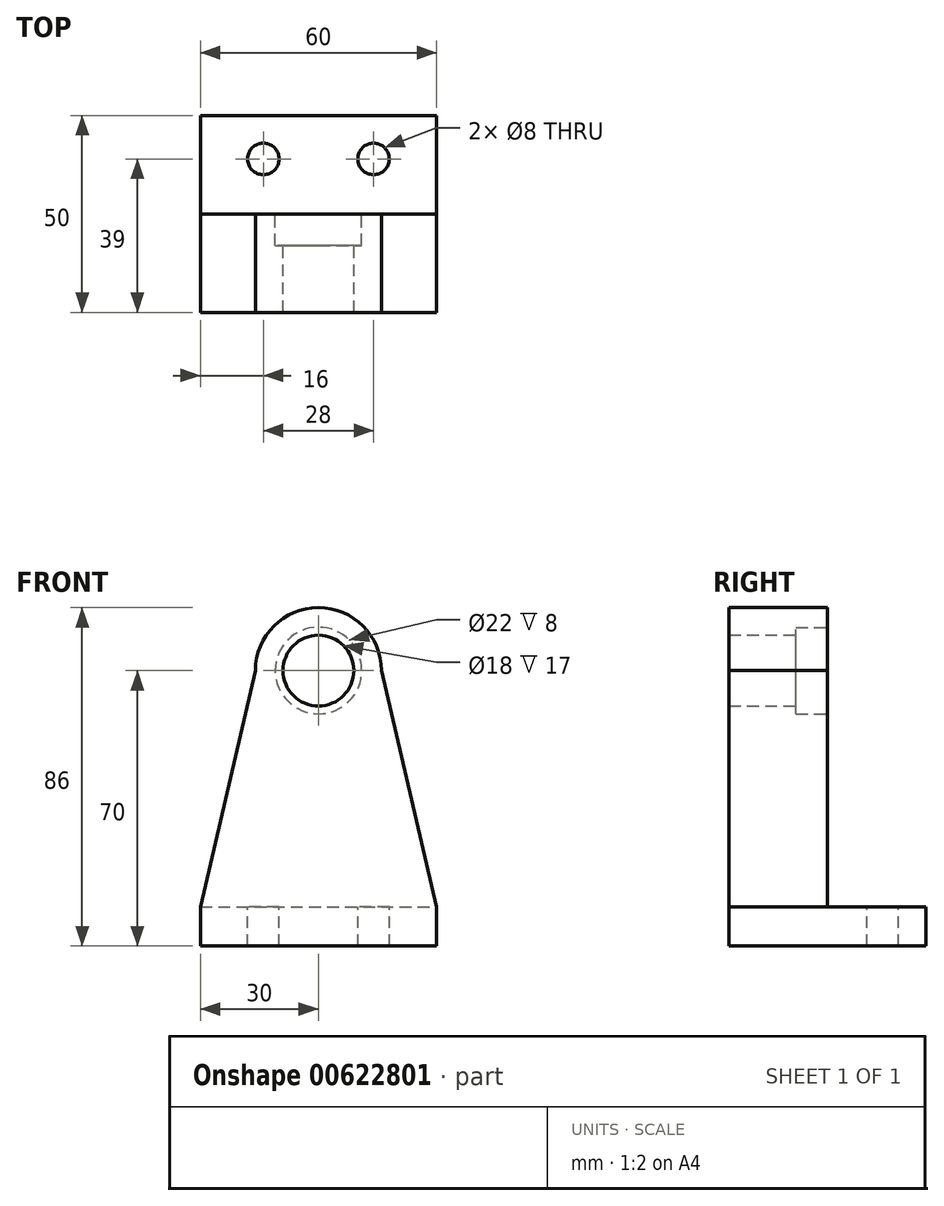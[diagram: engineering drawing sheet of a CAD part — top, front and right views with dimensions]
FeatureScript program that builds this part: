
annotation { "Feature Type Name" : "Feature", "Feature Type Description" : "" }
export const myFeature = defineFeature(function(context is Context, id is Id, definition is map)
    precondition{}
    {
        {
            var Q0;
            Q0=qCreatedBy(makeId("Front.planeOp"),FACE);
            var sketch = newSketch(context, id + "F0", { "sketchPlane" : qUnion([Q0])});
            skCircle(sketch, "E0", {"center": v(0, 0) * mm, "radius": 11 * mm});
            skCircle(sketch, "E1", {"center": v(0, 0) * mm, "radius": 9 * mm});
            skArc(sketch, "E2", {"start": v(-16, 0) * mm, "mid": v(0, 16) * mm, "end": v(16, 0) * mm});
            skLineSegment(sketch, "E3", {"start": v(-30, -60) * mm, "end": v(30, -60) * mm});
            skLineSegment(sketch, "E4", {"start": v(-16, 0) * mm, "end": v(-30, -60) * mm});
            skLineSegment(sketch, "E5", {"start": v(16, 0) * mm, "end": v(30, -60) * mm});
            skLineSegment(sketch, "E6", {"start": v(-30, -60) * mm, "end": v(-30, -70) * mm});
            skLineSegment(sketch, "E7", {"start": v(-30, -70) * mm, "end": v(30, -70) * mm});
            skLineSegment(sketch, "E8", {"start": v(30, -70) * mm, "end": v(30, -60) * mm});
            skSolve(sketch);
        }
        {
            var Q0;
            Q0 = qSketchRegion(id + "F0", true);
            extrude(context, id + "F1", {"entities" : qUnion([Q0]), "depth" : 25 * mm, "offsetDistance" : 25 * mm});
        }
        {
            var Q0;
            Q0=makeQuery(id+"F0.imprint","IMPRINT",FACE,{"disambiguationData":[TD([[makeQuery(id+"F0.imprint","IMPRINT",EDGE,{"derivedFrom":sQuery(id+"F0.wireOp",EDGE,"E3")}),-1.0]])]});
            extrude(context, id + "F2", {"entities" : qUnion([Q0]), "operationType" : NewBodyOperationType.ADD, "oppositeDirection" : true, "depth" : 25 * mm, "offsetDistance" : 25 * mm});
        }
        {
            var Q0;
            Q0=makeQuery(id+"F0.imprint","IMPRINT",FACE,{"disambiguationData":[TD([[makeQuery(id+"F0.imprint","IMPRINT",EDGE,{"derivedFrom":sQuery(id+"F0.wireOp",EDGE,"E0")}),1.0]])]});
            extrude(context, id + "F3", {"entities" : qUnion([Q0]), "operationType" : NewBodyOperationType.ADD, "depth" : 25 * mm, "offsetDistance" : 25 * mm, "hasSecondDirection" : true, "secondDirectionOppositeDirection" : false, "secondDirectionDepth" : 8 * mm});
        }
        {
            var Q0;
            Q0=makeQuery(id+"F2.opExtrude","SWEPT_FACE",FACE,{"disambiguationData":[OSD([sQuery(id+"F0.wireOp",EDGE,"E3")])]});
            var sketch = newSketch(context, id + "F4", { "sketchPlane" : qUnion([Q0])});
            skCircle(sketch, "E9", {"center": v(-14, 14) * mm, "radius": 4 * mm});
            skCircle(sketch, "E10", {"center": v(14, 14) * mm, "radius": 4 * mm});
            skSolve(sketch);
        }
        {
            var Q0;
            Q0=makeQuery(id+"F4.imprint","IMPRINT",FACE,{"disambiguationData":[TD([[makeQuery(id+"F4.imprint","IMPRINT",EDGE,{"derivedFrom":sQuery(id+"F4.wireOp",EDGE,"E9")}),1.0]])]});
            var Q1;
            Q1=makeQuery(id+"F4.imprint","IMPRINT",FACE,{"disambiguationData":[TD([[makeQuery(id+"F4.imprint","IMPRINT",EDGE,{"derivedFrom":sQuery(id+"F4.wireOp",EDGE,"E10")}),1.0]])]});
            extrude(context, id + "F5", {"entities" : qUnion([Q0, Q1]), "operationType" : NewBodyOperationType.REMOVE, "oppositeDirection" : true, "depth" : 25 * mm, "offsetDistance" : 25 * mm});
        }
    });
